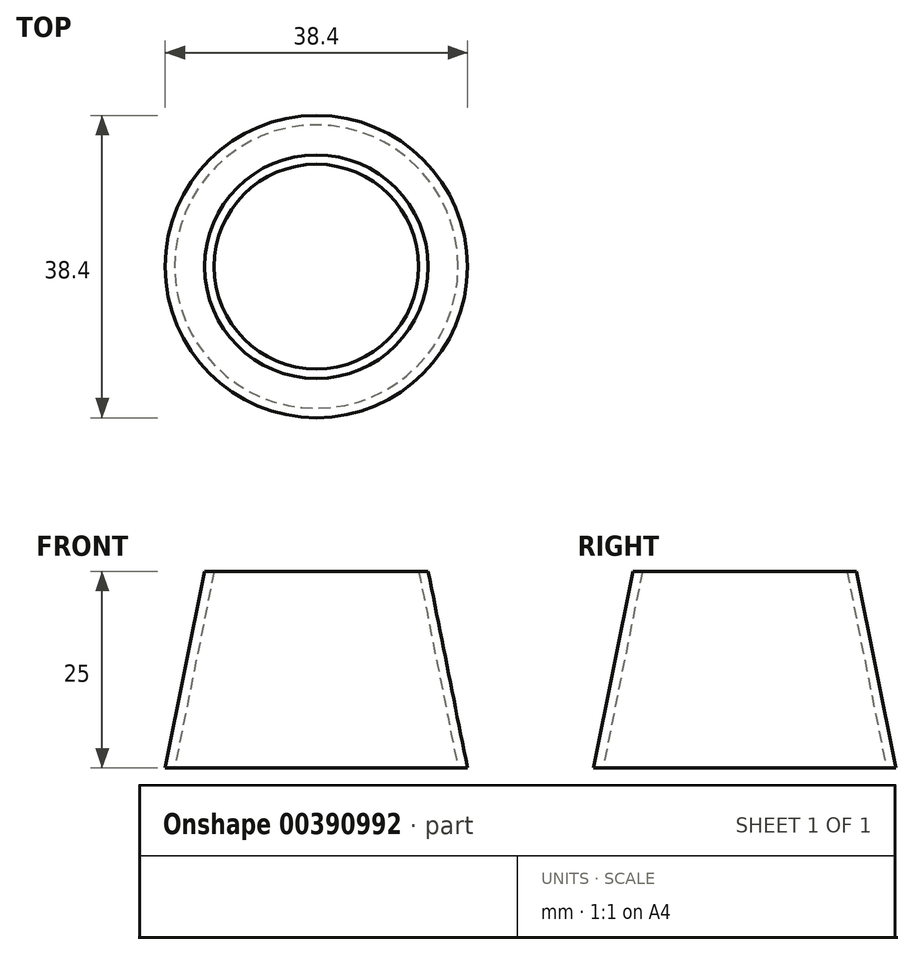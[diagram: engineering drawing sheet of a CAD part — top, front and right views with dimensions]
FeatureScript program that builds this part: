
annotation { "Feature Type Name" : "Feature", "Feature Type Description" : "" }
export const myFeature = defineFeature(function(context is Context, id is Id, definition is map)
    precondition{}
    {
        {
            var Q0;
            Q0=qCreatedBy(makeId("Top.planeOp"),FACE);
            var sketch = newSketch(context, id + "F0", { "sketchPlane" : qUnion([Q0])});
            skCircle(sketch, "E0", {"center": v(0, 0) * mm, "radius": 17.2 * mm});
            skSolve(sketch);
        }
        {
            var Q0;
            Q0=qCreatedBy(makeId("Top.planeOp"),FACE);
            var sketch = newSketch(context, id + "F1", { "sketchPlane" : qUnion([Q0])});
            skCircle(sketch, "E1", {"center": v(0, 0) * mm, "radius": 16 * mm});
            skSolve(sketch);
        }
        {
            var Q0;
            Q0=qCreatedBy(makeId("Top.planeOp"),FACE);
            cPlane(context, id + "F2", {"entities" : qUnion([Q0]), "cplaneType" : CPlaneType.OFFSET, "offset" : 10 * mm, "width" : 150 * mm, "height" : 150 * mm});
        }
        {
            var Q0;
            Q0=qCreatedBy(id+"F2.planeOp",FACE);
            var sketch = newSketch(context, id + "F3", { "sketchPlane" : qUnion([Q0])});
            skCircle(sketch, "E2.0", {"center": v(0, 0) * mm, "radius": 15.2 * mm});
            skSolve(sketch);
        }
        {
            var Q0;
            Q0=qCreatedBy(id+"F2.planeOp",FACE);
            var sketch = newSketch(context, id + "F4", { "sketchPlane" : qUnion([Q0])});
            skCircle(sketch, "E3.0", {"center": v(0, 0) * mm, "radius": 14 * mm});
            skSolve(sketch);
        }
        {
            var Q0;
            Q0=qCreatedBy(id+"F2.planeOp",FACE);
            cPlane(context, id + "F5", {"entities" : qUnion([Q0]), "cplaneType" : CPlaneType.OFFSET, "offset" : 5 * mm, "width" : 150 * mm, "height" : 150 * mm});
        }
        {
            var Q0;
            Q0=qCreatedBy(id+"F5.planeOp",FACE);
            var sketch = newSketch(context, id + "F6", { "sketchPlane" : qUnion([Q0])});
            skCircle(sketch, "E4.0", {"center": v(0, 0) * mm, "radius": 14.2 * mm});
            skSolve(sketch);
        }
        {
            var Q0;
            Q0=qCreatedBy(id+"F5.planeOp",FACE);
            var sketch = newSketch(context, id + "F7", { "sketchPlane" : qUnion([Q0])});
            skCircle(sketch, "E5.0", {"center": v(0, 0) * mm, "radius": 13 * mm});
            skSolve(sketch);
        }
        {
            var Q0;
            Q0=qCreatedBy(makeId("Top.planeOp"),FACE);
            cPlane(context, id + "F8", {"entities" : qUnion([Q0]), "cplaneType" : CPlaneType.OFFSET, "offset" : 10 * mm, "oppositeDirection" : true, "width" : 150 * mm, "height" : 150 * mm});
        }
        {
            var Q0;
            Q0=qCreatedBy(id+"F8.planeOp",FACE);
            var sketch = newSketch(context, id + "F9", { "sketchPlane" : qUnion([Q0])});
            skCircle(sketch, "E6.0", {"center": v(0, 0) * mm, "radius": 19.2 * mm});
            skSolve(sketch);
        }
        {
            var Q0;
            Q0=qCreatedBy(id+"F8.planeOp",FACE);
            var sketch = newSketch(context, id + "F10", { "sketchPlane" : qUnion([Q0])});
            skCircle(sketch, "E7.0", {"center": v(0, 0) * mm, "radius": 18 * mm});
            skSolve(sketch);
        }
        {
            var Q0;
            Q0 = qSketchRegion(id + "F9", true);
            var Q1;
            Q1 = qSketchRegion(id + "F0", true);
            var Q2;
            Q2 = qSketchRegion(id + "F3", true);
            var Q3;
            Q3 = qSketchRegion(id + "F6", true);
            loft(context, id + "F11", {"sheetProfilesArray" : [{ "sheetProfileEntities" : qUnion([Q0]) }, { "sheetProfileEntities" : qUnion([Q1]) }, { "sheetProfileEntities" : qUnion([Q2]) }, { "sheetProfileEntities" : qUnion([Q3]) }]});
        }
        {
            var Q1;
            Q1 = qSketchRegion(id + "F10", true);
            var Q2;
            Q2 = qSketchRegion(id + "F1", true);
            var Q3;
            Q3 = qSketchRegion(id + "F4", true);
            var Q4;
            Q4 = qSketchRegion(id + "F7", true);
            loft(context, id + "F12", {"operationType" : NewBodyOperationType.REMOVE, "sheetProfilesArray" : [{ "sheetProfileEntities" : qUnion([Q1]) }, { "sheetProfileEntities" : qUnion([Q2]) }, { "sheetProfileEntities" : qUnion([Q3]) }, { "sheetProfileEntities" : qUnion([Q4]) }]});
        }
    });
